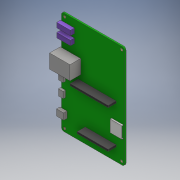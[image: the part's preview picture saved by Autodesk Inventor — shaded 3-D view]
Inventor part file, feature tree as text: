
AUTODESK INVENTOR PART (.ipt)
format: ipt  version: 2019 (Build 230136000, 136)  size: 414,720 bytes
history: native  units: mm
features: extrude x13, sketch x13, other x1, fillet x1
ambient origin geometry x8: Origin, YZ Plane, XZ Plane, XY Plane, X Axis, Y Axis, Z Axis, Center Point
bodies: Solide1 (feature_tree)
feature tree (28):
  other  "STM32F746G-Disco"
  extrude  "Extrusion1"  Depth=130.0mm
  extrude  "Extrusion2"  Depth=80.0mm
  fillet  "Congé1"  Radius=40.0mm
  extrude  "Extrusion3"  Depth=65.0mm
  extrude  "Extrusion4"  Depth=1.6mm TaperAngle=0.0deg
  extrude  "Extrusion5"  Depth=3.2mm
  extrude  "Extrusion6"  Depth=3.2mm
  extrude  "Extrusion7"  Depth=3.2mm
  extrude  "Extrusion8"  Depth=3.2mm
  extrude  "Extrusion9"  Depth=122.0mm
  extrude  "Extrusion10"  Depth=122.0mm
  extrude  "Extrusion11"  Depth=72.0mm
  extrude  "Extrusion12"  Depth=72.0mm
  extrude  "Extrusion13"  Depth=61.0mm
  sketch  "Esquisse1"
  sketch  "Esquisse2"
  sketch  "Esquisse3"
  sketch  "Esquisse4"
  sketch  "Esquisse5"
  sketch  "Esquisse6"
  sketch  "Esquisse7"
  sketch  "Esquisse8"
  sketch  "Esquisse9"
  sketch  "Esquisse10"
  sketch  "Esquisse11"
  sketch  "Esquisse13"
  sketch  "Esquisse14"
